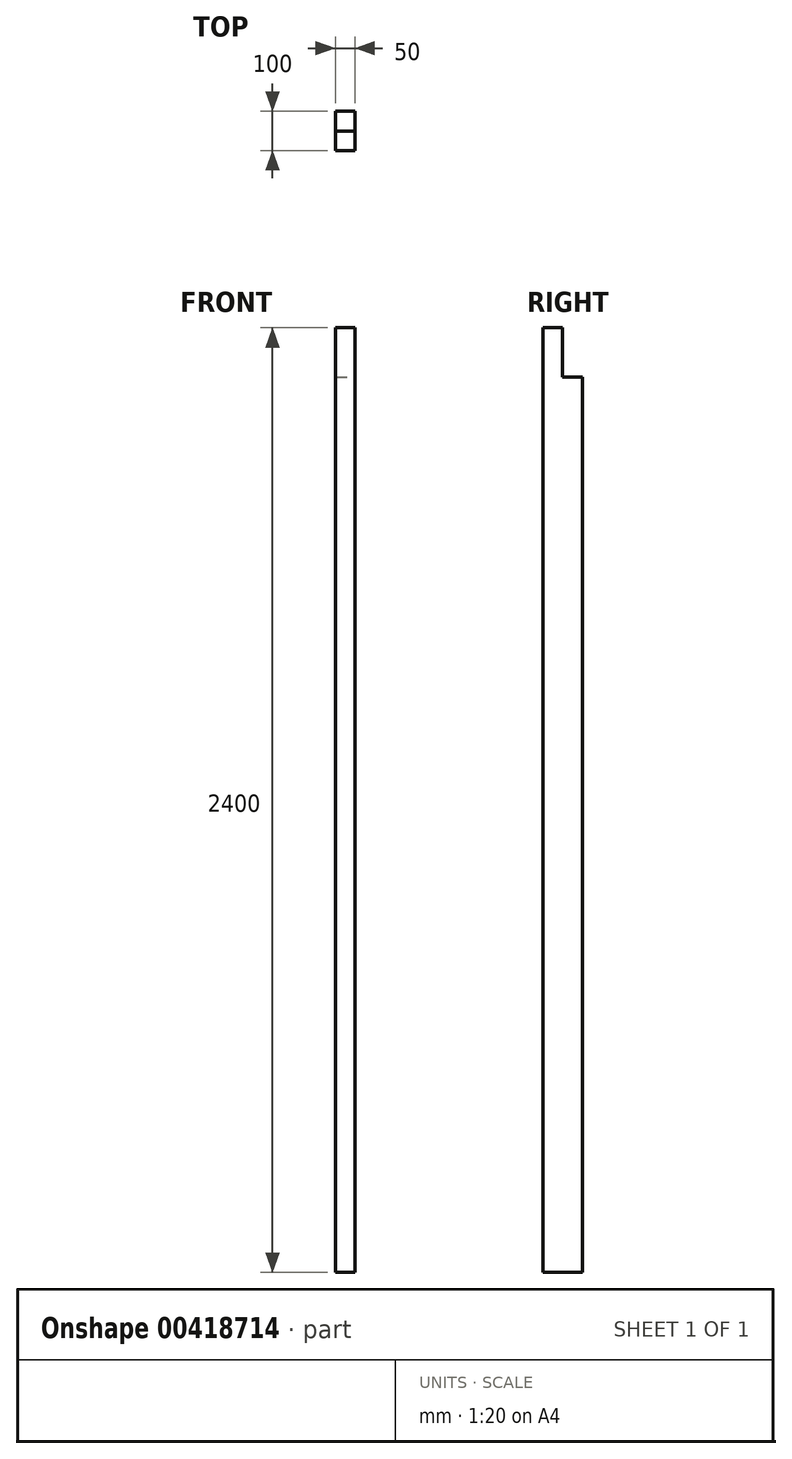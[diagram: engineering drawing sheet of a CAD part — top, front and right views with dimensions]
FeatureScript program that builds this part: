
annotation { "Feature Type Name" : "Feature", "Feature Type Description" : "" }
export const myFeature = defineFeature(function(context is Context, id is Id, definition is map)
    precondition{}
    {
        {
            var Q0;
            Q0=qCreatedBy(makeId("Top.planeOp"),FACE);
            var sketch = newSketch(context, id + "F0", { "sketchPlane" : qUnion([Q0])});
            skLineSegment(sketch, "E0.bottom", {"start": v(25, 50) * mm, "end": v(-25, 50) * mm});
            skLineSegment(sketch, "E0.top", {"start": v(25, -50) * mm, "end": v(-25, -50) * mm});
            skLineSegment(sketch, "E0.left", {"start": v(25, 50) * mm, "end": v(25, -50) * mm});
            skLineSegment(sketch, "E0.right", {"start": v(-25, 50) * mm, "end": v(-25, -50) * mm});
            skPoint(sketch, "E0.middle", {"position": v(0, 0) * mm});
            skSolve(sketch);
        }
        {
            var Q0;
            Q0 = qSketchRegion(id + "F0", true);
            extrude(context, id + "F1", {"entities" : qUnion([Q0]), "depth" : 2400 * mm});
        }
        {
            var Q0;
            Q0=qCreatedBy(makeId("Right.planeOp"),FACE);
            var sketch = newSketch(context, id + "F2", { "sketchPlane" : qUnion([Q0])});
            skLineSegment(sketch, "E1.bottom", {"start": v(0, 2275) * mm, "end": v(50, 2275) * mm});
            skLineSegment(sketch, "E1.top", {"start": v(0, 2400) * mm, "end": v(50, 2400) * mm});
            skLineSegment(sketch, "E1.left", {"start": v(0, 2275) * mm, "end": v(0, 2400) * mm});
            skLineSegment(sketch, "E1.right", {"start": v(50, 2275) * mm, "end": v(50, 2400) * mm});
            skSolve(sketch);
        }
        {
            var Q0;
            Q0 = qSketchRegion(id + "F2", true);
            extrude(context, id + "F3", {"entities" : qUnion([Q0]), "operationType" : NewBodyOperationType.REMOVE, "endBound" : BoundingType.UP_TO_NEXT, "oppositeDirection" : true, "depth" : 25 * mm, "hasSecondDirection" : true, "secondDirectionBound" : SecondDirectionBoundingType.UP_TO_NEXT, "secondDirectionOppositeDirection" : false, "secondDirectionDepth" : 25 * mm});
        }
    });
